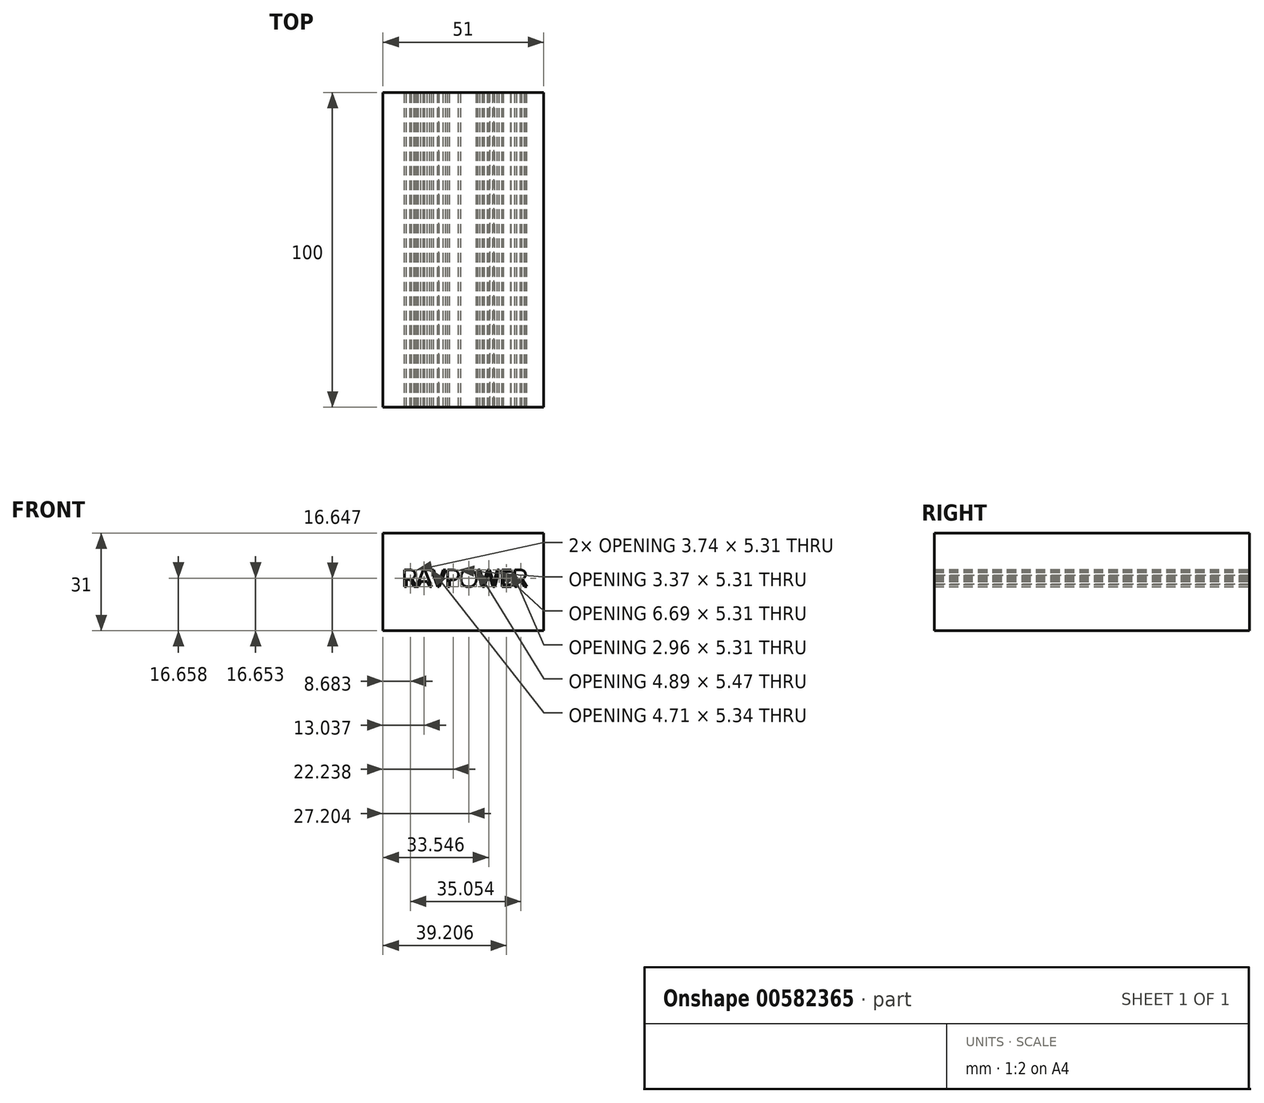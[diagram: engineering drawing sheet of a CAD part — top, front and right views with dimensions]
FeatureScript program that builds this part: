
annotation { "Feature Type Name" : "Feature", "Feature Type Description" : "" }
export const myFeature = defineFeature(function(context is Context, id is Id, definition is map)
    precondition{}
    {
        {
            var Q0;
            Q0=qCreatedBy(makeId("Front.planeOp"),FACE);
            var sketch = newSketch(context, id + "F0", { "sketchPlane" : qUnion([Q0])});
            skLineSegment(sketch, "E0.bottom", {"start": v(-66.8, 64.81) * mm, "end": v(-15.8, 64.81) * mm});
            skLineSegment(sketch, "E0.top", {"start": v(-66.8, 33.81) * mm, "end": v(-15.8, 33.81) * mm});
            skLineSegment(sketch, "E0.left", {"start": v(-66.8, 64.81) * mm, "end": v(-66.8, 33.81) * mm});
            skLineSegment(sketch, "E0.right", {"start": v(-15.8, 64.81) * mm, "end": v(-15.8, 33.81) * mm});
            skText(sketch, "E1", { "text": "RAVPOWER", "fontName": "OpenSans-Regular.ttf"});
            const initialGuessF0  = {"E1": [-0.06072, 0.0478, 1, 0, 0.00536]};
            skSetInitialGuess(sketch, initialGuessF0);
            skSolve(sketch);
        }
        {
            var Q0;
            Q0 = qSketchRegion(id + "F0", true);
            var Q1;
            Q1=makeQuery(id+"F0.imprint","IMPRINT",FACE,{"disambiguationData":[TD([[makeQuery(id+"F0.imprint","IMPRINT",EDGE,{"derivedFrom":sQuery(id+"F0.wireOp",EDGE,"E0.bottom")}),-1.0]])]});
            extrude(context, id + "F1", {"entities" : qUnion([Q0, Q1]), "depth" : 100 * mm, "offsetDistance" : 25 * mm});
        }
    });
